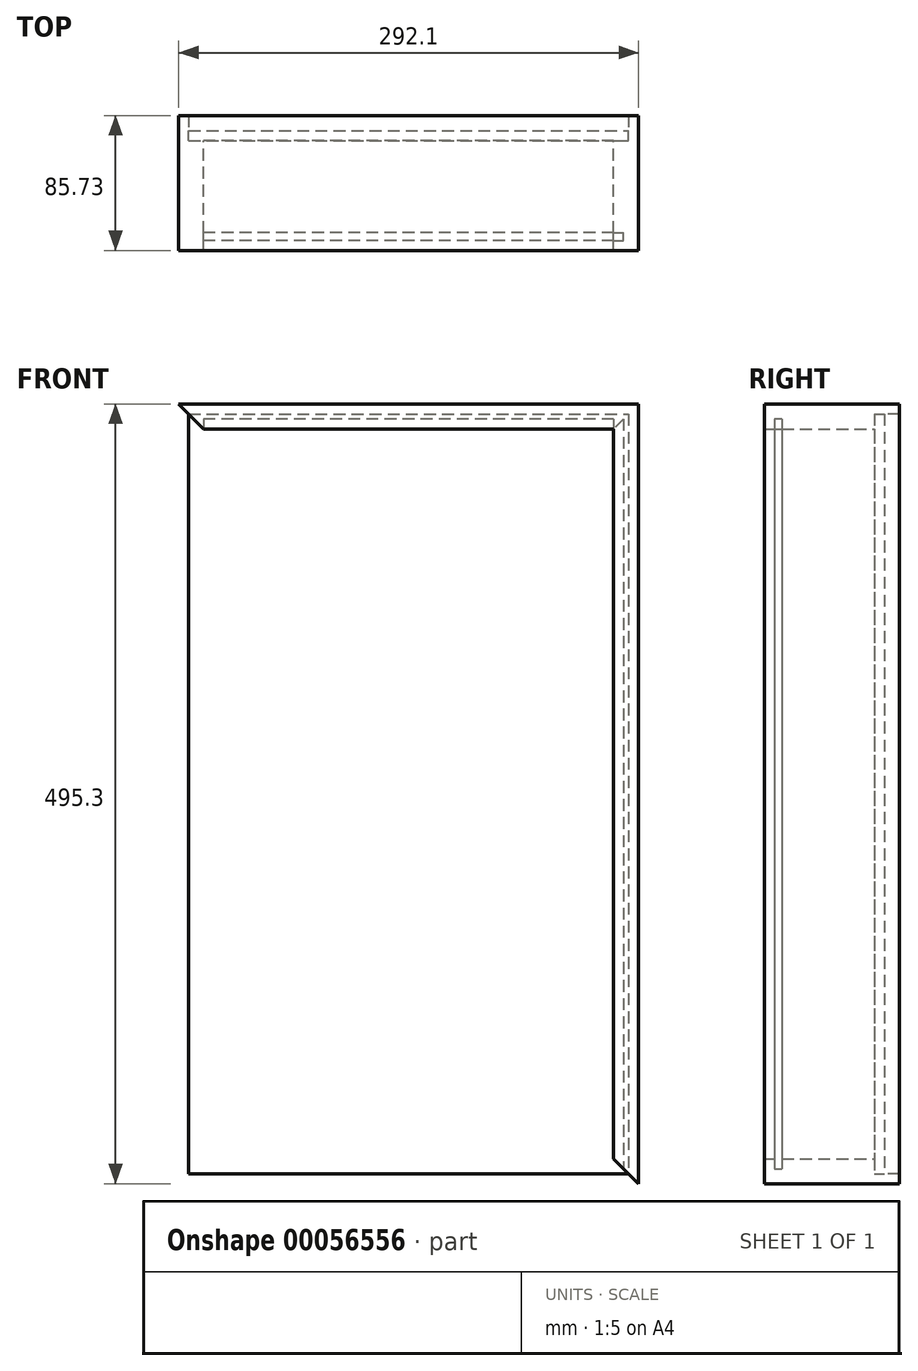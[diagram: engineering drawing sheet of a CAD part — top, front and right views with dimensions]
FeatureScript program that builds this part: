
annotation { "Feature Type Name" : "Feature", "Feature Type Description" : "" }
export const myFeature = defineFeature(function(context is Context, id is Id, definition is map)
    precondition{}
    {
        {
            var Q0;
            Q0=qCreatedBy(makeId("Front.planeOp"),FACE);
            var sketch = newSketch(context, id + "F0", { "sketchPlane" : qUnion([Q0])});
            skLineSegment(sketch, "E0.bottom", {"start": v(0, 0) * mm, "end": v(279.4, 0) * mm});
            skLineSegment(sketch, "E0.top", {"start": v(0, -482.6) * mm, "end": v(279.4, -482.6) * mm});
            skLineSegment(sketch, "E0.left", {"start": v(0, 0) * mm, "end": v(0, -482.6) * mm});
            skLineSegment(sketch, "E0.right", {"start": v(279.4, 0) * mm, "end": v(279.4, -482.6) * mm});
            skLineSegment(sketch, "E1", {"start": v(139.7, 66.07) * mm, "end": v(139.7, -554.15) * mm, "construction": true});
            skPoint(sketch, "E1.startSnap0", {"position": v(139.7, 0) * mm});
            skPoint(sketch, "E1.endSnap0", {"position": v(139.7, -482.6) * mm});
            skLineSegment(sketch, "E2", {"start": v(-75.71, -241.3) * mm, "end": v(332.06, -241.3) * mm, "construction": true});
            skPoint(sketch, "E2.startSnap0", {"position": v(0, -241.3) * mm});
            skSolve(sketch);
        }
        {
            var Q0;
            Q0=makeQuery(id+"F0.imprint","IMPRINT",FACE,{"disambiguationData":[TD([[makeQuery(id+"F0.imprint","IMPRINT",EDGE,{"derivedFrom":sQuery(id+"F0.wireOp",EDGE,"E0.bottom")}),-1.0]])]});
            extrude(context, id + "F1", {"entities" : qUnion([Q0]), "depth" : 6.35 * mm});
        }
        {
            var Q0;
            Q0=qCreatedBy(makeId("Front.planeOp"),FACE);
            var sketch = newSketch(context, id + "F2", { "sketchPlane" : qUnion([Q0])});
            skLineSegment(sketch, "E3", {"start": v(269.87, -9.53) * mm, "end": v(285.75, 6.35) * mm});
            skLineSegment(sketch, "E4", {"start": v(285.75, 6.35) * mm, "end": v(285.75, -488.95) * mm});
            skLineSegment(sketch, "E5", {"start": v(285.75, -488.95) * mm, "end": v(269.88, -473.07) * mm});
            skLineSegment(sketch, "E6", {"start": v(269.88, -473.07) * mm, "end": v(269.88, -9.53) * mm});
            skLineSegment(sketch, "E7", {"start": v(279.4, 0) * mm, "end": v(279.4, -482.6) * mm});
            skLineSegment(sketch, "E8", {"start": v(269.88, -473.07) * mm, "end": v(279.4, -473.07) * mm, "construction": true});
            skLineSegment(sketch, "E9", {"start": v(279.4, -473.07) * mm, "end": v(285.75, -473.07) * mm, "construction": true});
            skPoint(sketch, "E10", {"position": v(-314.85, -119.7) * mm});
            skPoint(sketch, "E11", {"position": v(139.7, 0) * mm});
            skLineSegment(sketch, "E12", {"start": v(139.7, 75.86) * mm, "end": v(139.7, -512.29) * mm, "construction": true});
            skLineSegment(sketch, "E13.MirrorCS", {"start": v(-6.35, -488.95) * mm, "end": v(9.52, -473.07) * mm});
            skLineSegment(sketch, "E14.MirrorCS", {"start": v(0, 0) * mm, "end": v(0, -482.6) * mm});
            skLineSegment(sketch, "E15.MirrorCS", {"start": v(9.53, -9.53) * mm, "end": v(-6.35, 6.35) * mm});
            skLineSegment(sketch, "E16.MirrorCS", {"start": v(9.53, -473.07) * mm, "end": v(9.53, -9.53) * mm});
            skLineSegment(sketch, "E17.MirrorCS", {"start": v(-6.35, 6.35) * mm, "end": v(-6.35, -488.95) * mm});
            skLineSegment(sketch, "E18", {"start": v(9.52, -473.07) * mm, "end": v(269.88, -473.07) * mm});
            skLineSegment(sketch, "E19", {"start": v(-6.35, -488.95) * mm, "end": v(285.75, -488.95) * mm});
            skLineSegment(sketch, "E20", {"start": v(9.53, -9.53) * mm, "end": v(269.88, -9.53) * mm});
            skLineSegment(sketch, "E21", {"start": v(-6.35, 6.35) * mm, "end": v(285.75, 6.35) * mm});
            skLineSegment(sketch, "E22", {"start": v(0, 0) * mm, "end": v(279.4, 0) * mm});
            skLineSegment(sketch, "E23", {"start": v(0, -482.6) * mm, "end": v(279.4, -482.6) * mm});
            skSolve(sketch);
        }
        {
            var Q0;
            {var subQ0=sQuery(id+"F2.wireOp",EDGE,"E6");Q0=makeQuery(id+"F2.imprint","IMPRINT",FACE,{"disambiguationData":[TD([[makeQuery(id+"F2.imprint","IMPRINT",EDGE,{"derivedFrom":subQ0}),-1.0]])]});}
            var Q1;
            {var subQ0=sQuery(id+"F2.wireOp",EDGE,"E4");Q1=makeQuery(id+"F2.imprint","IMPRINT",FACE,{"disambiguationData":[TD([[makeQuery(id+"F2.imprint","IMPRINT",EDGE,{"derivedFrom":subQ0}),-1.0]])]});}
            extrude(context, id + "F3", {"entities" : qUnion([Q0, Q1]), "depth" : 76.2 * mm});
        }
        {
            var Q0;
            {var subQ0=sQuery(id+"F2.wireOp",EDGE,"E4");Q0=makeQuery(id+"F2.imprint","IMPRINT",FACE,{"disambiguationData":[TD([[makeQuery(id+"F2.imprint","IMPRINT",EDGE,{"derivedFrom":subQ0}),-1.0]])]});}
            extrude(context, id + "F4", {"entities" : qUnion([Q0]), "operationType" : NewBodyOperationType.ADD, "oppositeDirection" : true, "depth" : 9.52 * mm});
        }
        {
            var Q0;
            Q0=makeQuery(id+"F3.opExtrude","SWEPT_FACE",FACE,{"disambiguationData":[OSD([sQuery(id+"F2.wireOp",EDGE,"E6")])]});
            var sketch = newSketch(context, id + "F5", { "sketchPlane" : qUnion([Q0])});
            skLineSegment(sketch, "E24", {"start": v(69.85, 0) * mm, "end": v(69.85, -473.07) * mm});
            skLineSegment(sketch, "E25", {"start": v(69.85, -473.07) * mm, "end": v(65.07, -473.07) * mm});
            skLineSegment(sketch, "E26", {"start": v(65.07, -473.07) * mm, "end": v(65.07, 0) * mm});
            skLineSegment(sketch, "E27", {"start": v(65.07, 0) * mm, "end": v(69.85, 0) * mm});
            skPoint(sketch, "E28", {"position": v(65.07, -9.53) * mm});
            skPoint(sketch, "E29", {"position": v(69.85, -9.53) * mm});
            skPoint(sketch, "E30", {"position": v(76.2, -9.53) * mm});
            skLineSegment(sketch, "E31", {"start": v(65.07, -473.07) * mm, "end": v(65.07, -482.6) * mm});
            skLineSegment(sketch, "E32", {"start": v(69.85, -473.07) * mm, "end": v(69.85, -482.6) * mm});
            skLineSegment(sketch, "E33", {"start": v(69.85, -482.6) * mm, "end": v(65.07, -482.6) * mm});
            skPoint(sketch, "E34.orphan", {"position": v(60.3, -482.6) * mm});
            skSolve(sketch);
        }
        {
            var Q0;
            Q0 = qSketchRegion(id + "F5", true);
            extrude(context, id + "F6", {"entities" : qUnion([Q0]), "operationType" : NewBodyOperationType.REMOVE, "oppositeDirection" : true, "depth" : 6.35 * mm});
        }
        {
            var Q0;
            {var subQ0=sQuery(id+"F2.wireOp",EDGE,"E20");Q0=makeQuery(id+"F2.imprint","IMPRINT",FACE,{"disambiguationData":[TD([[makeQuery(id+"F2.imprint","IMPRINT",EDGE,{"derivedFrom":subQ0}),1.0]])]});}
            var Q1;
            {var subQ0=sQuery(id+"F2.wireOp",EDGE,"E21");Q1=makeQuery(id+"F2.imprint","IMPRINT",FACE,{"disambiguationData":[TD([[makeQuery(id+"F2.imprint","IMPRINT",EDGE,{"derivedFrom":subQ0}),-1.0]])]});}
            extrude(context, id + "F7", {"entities" : qUnion([Q0, Q1]), "depth" : 76.2 * mm});
        }
        {
            var Q0;
            {var subQ0=sQuery(id+"F2.wireOp",EDGE,"E21");Q0=makeQuery(id+"F2.imprint","IMPRINT",FACE,{"disambiguationData":[TD([[makeQuery(id+"F2.imprint","IMPRINT",EDGE,{"derivedFrom":subQ0}),-1.0]])]});}
            extrude(context, id + "F8", {"entities" : qUnion([Q0]), "operationType" : NewBodyOperationType.ADD, "oppositeDirection" : true, "depth" : 9.52 * mm});
        }
        {
            var Q0;
            Q0=makeQuery(id+"F7.opExtrude","SWEPT_FACE",FACE,{"disambiguationData":[OSD([sQuery(id+"F2.wireOp",EDGE,"E20")])]});
            var sketch = newSketch(context, id + "F9", { "sketchPlane" : qUnion([Q0])});
            skLineSegment(sketch, "E35", {"start": v(269.88, 76.2) * mm, "end": v(9.53, 76.2) * mm});
            skLineSegment(sketch, "E36", {"start": v(9.53, 76.2) * mm, "end": v(9.53, 65.07) * mm});
            skLineSegment(sketch, "E37", {"start": v(269.88, 76.2) * mm, "end": v(269.88, 65.07) * mm});
            skLineSegment(sketch, "E38", {"start": v(269.88, 69.85) * mm, "end": v(9.53, 69.85) * mm});
            skLineSegment(sketch, "E39", {"start": v(269.87, 65.07) * mm, "end": v(9.53, 65.07) * mm});
            skLineSegment(sketch, "E40", {"start": v(269.88, 65.07) * mm, "end": v(285.75, 65.07) * mm});
            skLineSegment(sketch, "E41", {"start": v(269.88, 69.85) * mm, "end": v(285.75, 69.85) * mm});
            skLineSegment(sketch, "E42", {"start": v(285.75, 69.85) * mm, "end": v(285.75, 65.07) * mm});
            skLineSegment(sketch, "E43", {"start": v(9.53, 65.07) * mm, "end": v(-6.35, 65.07) * mm});
            skLineSegment(sketch, "E44", {"start": v(9.53, 69.85) * mm, "end": v(-6.35, 69.85) * mm});
            skLineSegment(sketch, "E45", {"start": v(-6.35, 65.07) * mm, "end": v(-6.35, 69.85) * mm});
            skSolve(sketch);
        }
        {
            var Q0;
            {var subQ0=sQuery(id+"F9.wireOp",EDGE,"E38");var subQ1=sQuery(id+"F2.wireOp",EDGE,"E20");var subQ2=makeQuery(id+"F7.opExtrude","SWEPT_EDGE",EDGE,{"disambiguationData":[OSD([sQuery(id+"F2.wireOp",EDGE,"E3"),sQuery(id+"F2.wireOp",EDGE,"E6"),subQ1])]});var subQ3=makeQuery(id+"F9.imprint","INTERSECT",VERTEX,{"derivedFrom":[subQ2,subQ0]});Q0=makeQuery(id+"F9.imprint","IMPRINT",FACE,{"disambiguationData":[TD([[makeQuery(id+"F9.imprint","IMPRINT",EDGE,{"disambiguationData":[TD([[subQ3,-1.0]])],"derivedFrom":subQ0}),1.0]])]});}
            var Q1;
            {var subQ0=sQuery(id+"F9.wireOp",EDGE,"E39");var subQ1=sQuery(id+"F9.wireOp",EDGE,"E36");var subQ2=makeQuery(id+"F9.imprint","INTERSECT",VERTEX,{"derivedFrom":[subQ1,subQ0]});Q1=makeQuery(id+"F9.imprint","IMPRINT",FACE,{"disambiguationData":[TD([[makeQuery(id+"F9.imprint","IMPRINT",EDGE,{"disambiguationData":[TD([[subQ2,1.0]])],"derivedFrom":subQ1}),1.0]])]});}
            var Q2;
            {var subQ0=sQuery(id+"F9.wireOp",EDGE,"E39");var subQ1=sQuery(id+"F9.wireOp",EDGE,"E37");var subQ2=makeQuery(id+"F9.imprint","INTERSECT",VERTEX,{"derivedFrom":[subQ1,subQ0]});Q2=makeQuery(id+"F9.imprint","IMPRINT",FACE,{"disambiguationData":[TD([[makeQuery(id+"F9.imprint","IMPRINT",EDGE,{"disambiguationData":[TD([[subQ2,1.0]])],"derivedFrom":subQ1}),-1.0]])]});}
            extrude(context, id + "F10", {"entities" : qUnion([Q0, Q1, Q2]), "operationType" : NewBodyOperationType.REMOVE, "oppositeDirection" : true, "depth" : 6.35 * mm});
        }
    });
